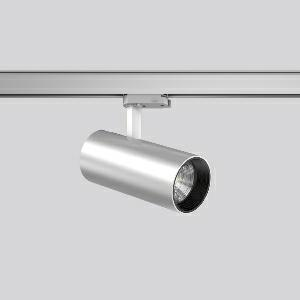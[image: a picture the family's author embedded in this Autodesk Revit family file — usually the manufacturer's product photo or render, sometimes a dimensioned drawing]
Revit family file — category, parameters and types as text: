
# Revit family: deecos_s_mini_742201_004_2_76_0138
name_source: partatom
category: Lighting Fixtures
units: mm (PartAtom-declared; Revit-internal decimal feet)

## family parameters
Cut with Voids When Loaded = No
Host = Face
Light Source = No
Part Type = Normal
Room Calculation Point = No
Round Connector Dimension = Use Diameter
Shared = No

## types (1)
- DEECOS S mini (1 x LED Modul 927, 2150 lm, 2700)
    Apparent Load = 20 VA
    Approval mark = CE
    CIE Flux Codes = 80 99 100 100 100
    Color Rendering = 92
    Color Temperature = 2700
    Default Elevation = 1800 mm
    Description = Series: DEECOS S mini
LED surface-mounted projector in modern design with no visible cooling ribs. Housing: die-cast aluminium, powder-coated. Rotation range: 356°. Swivel range: 90°. Black plastic ring and recessed LED to prevent glare from the side. Optical assembly with lens made of plastic (polycarbonate) for the best homogeneous light distribution - can be changed without tools. Best colour rendering index Ra>90. With adapter for RZB 3-circuit DALI tracks. Suitable for Track on ceiling, Wall track. High quality converter without flickering and stroboscopic effect. The following accessories can be mounted without use of tools: interchangeable lenses, decorative glasses, honeycomb louvre, clear and frosted diffusers, white interchangeable plastic ring. 
Colour: silver
Diameter: 87 mm
Height: 214 mm
Lamp: LED
Socket: without socket
Colour temperature: 2700K
Colour rendering index (CRI): 92
System power: 20 W
Rated luminous flux: 2150 lm
Luminous efficiency: 108 lm/W
Control gear: Converter, dimmable, DALI
Protection class: I
Type of protection: IP 20
    Height = 214 mm
    Lamp = 1 x LED Modul 927
    Lamp Light Flux = 2150 lm
    Lamp count = 1
    Length = 87 mm
    Lifetime = 50000 h
    Luminous efficacy = 108 lm/W
    Manufacturer = RZB
    ModVariant = No
    Model = 742201.004.2.76
    Mounting Place = Ceiling
    Mounting Type = Rail mounted
    Number of Poles = 1
    OnlyDefault = Yes
    Power Factor = 1
    Product Name = DEECOS S mini
    Product group = Track mounted projectors
    ProductGroupID = 301
    Protection Class = Protection class I
    Protection Degree = IP 20
    RLX_Detail_Level = 1
    RLX_Emergency_Light_Flux = 0 lm
    RLX_Emergency_Type = 0
    RLX_Emergency_Type_DB = No
    RlxData = <blob elided: 37649 chars, md5=72c619c0>
    Socket = socket
    Standby Power = 0 W
    System Light Flux = 2150 lm
    System Power = 20 W
    Type Comments = Product without accessories
    Type Image = 741930.004.jpg
    URL = http://relux.com
    VarID = ---
    Voltage = 230 V
    Voltage Range = 220-240 V
    Weight = 0.00 kg
    Width = 0 mm  [stored 0 ft]

note: [stored X ft] marks values corroborated as IEEE doubles in the binary element streams (Revit-internal decimal feet)

## geometry (parser evidence)
native form markers: Blend x4, Sweep x10
no freeform markers — native parametric forms only
